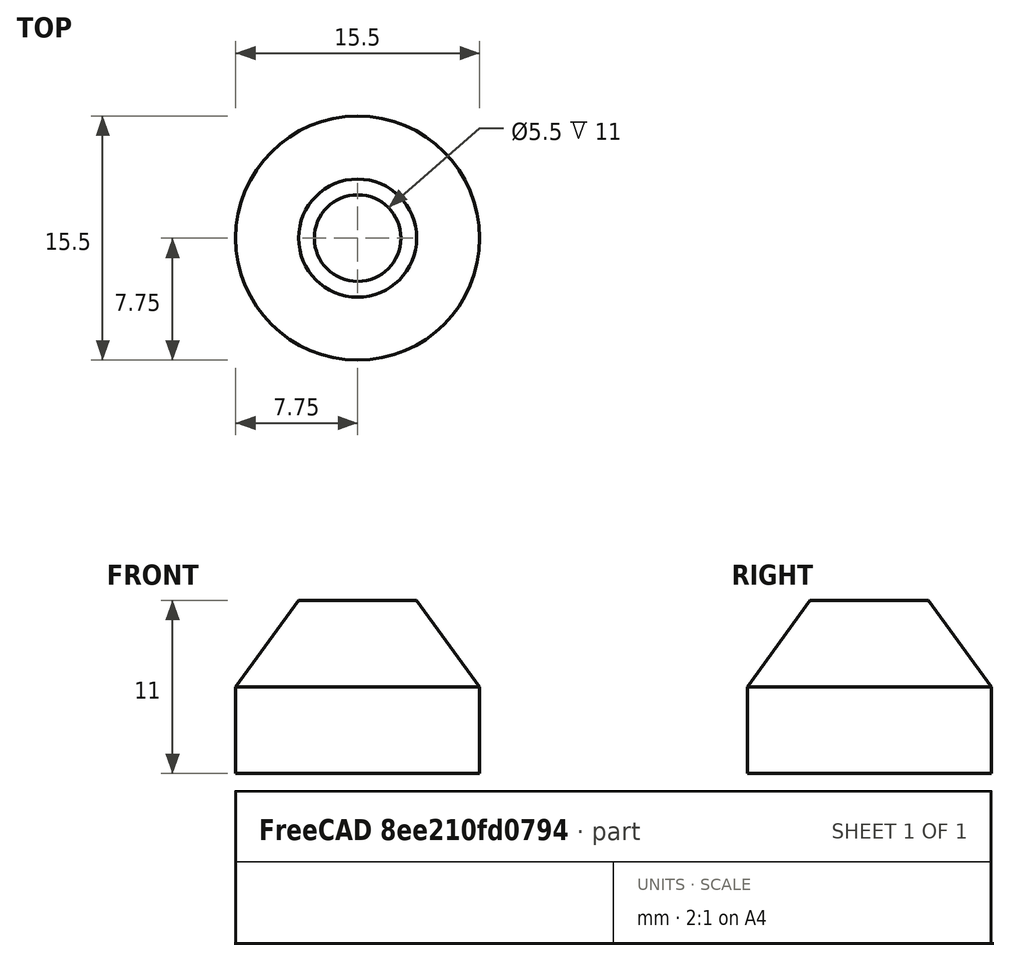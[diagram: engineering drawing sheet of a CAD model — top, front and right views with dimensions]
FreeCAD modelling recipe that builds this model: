
FCSTD DOCUMENT  (FreeCAD 0.19R)
Label: x-axis-roller-spacer
License: All rights reserved
LicenseURL: http://en.wikipedia.org/wiki/All_rights_reserved
objects: Sketcher::SketchObject×1, PartDesign::Revolution×1, PartDesign::Body×1
note: 4 computed .brp shape members not serialized (recipe doc carries the construction recipe); baked Part::Feature solids carry a one-line shape summary decoded from their .brp

FEATURE [Sketcher::SketchObject] Sketch
  FullyConstrained = true
  MapMode = 5
  Placement = pos=(0,0,0) rot=(1,0,0;1.5708rad)
  Support = -> [XZ_Plane]
  sketch-geometry (5):
    g0: LineSegment StartX=2.75 StartY=0 StartZ=0 EndX=2.75 EndY=11 EndZ=0
    g1: LineSegment StartX=2.75 StartY=11 StartZ=0 EndX=3.75 EndY=11 EndZ=0
    g2: LineSegment StartX=3.75 StartY=11 StartZ=0 EndX=7.75 EndY=5.5 EndZ=0
    g3: LineSegment StartX=7.75 StartY=5.5 StartZ=0 EndX=7.75 EndY=0 EndZ=0
    g4: LineSegment StartX=7.75 StartY=0 StartZ=0 EndX=2.75 EndY=0 EndZ=0
  constraints (15):
    c: PointOnObject(g0,g-1)
    c: Vertical(g0)
    c: Coincident(g1,g0)
    c: Horizontal(g1)
    c: Coincident(g2,g1)
    c: Coincident(g3,g2)
    c: PointOnObject(g3,g-1)
    c: Vertical(g3)
    c: Coincident(g4,g3)
    c: Coincident(g4,g0)
    c: DistanceY(g3,g3) = 5.5
    c: DistanceY(g0,g0) = 11
    c: DistanceX(g-1,g0) = 2.75
    c: DistanceX(g4,g4) = 5
    c: DistanceX(g1,g1) = 1
FEATURE [PartDesign::Revolution] Revolution
  Angle = 360
  Axis = (0,-2e-16,1)
  Base = (0,0,0)
  Placement = pos=(0,0,0) rot=(1,0,0;1.5708rad)
  Profile = -> Sketch
  ReferenceAxis = -> Sketch [V_Axis]
  Reversed = true
FEATURE [PartDesign::Body] Body
  Group = -> [Sketch,Revolution]
  Origin = -> Origin
  Tip = -> Revolution
